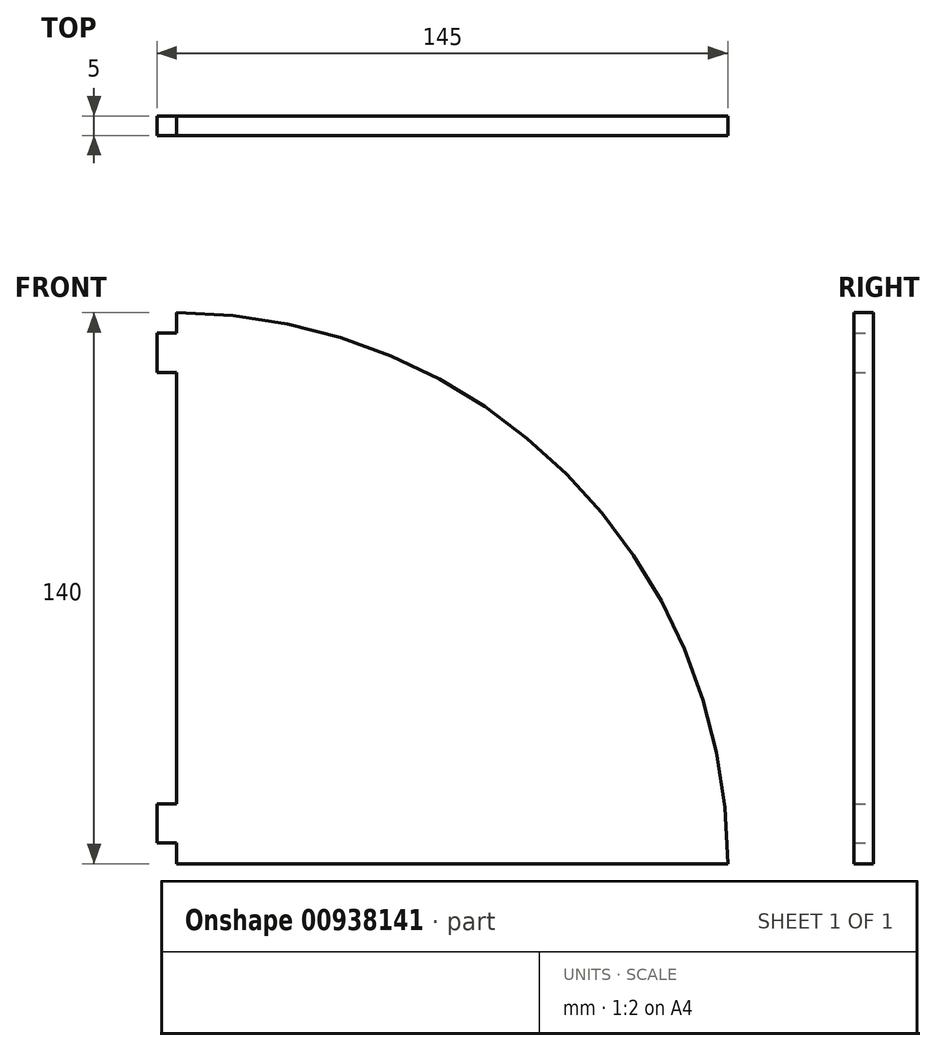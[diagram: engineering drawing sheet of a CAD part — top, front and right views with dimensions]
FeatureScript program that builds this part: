
annotation { "Feature Type Name" : "Feature", "Feature Type Description" : "" }
export const myFeature = defineFeature(function(context is Context, id is Id, definition is map)
    precondition{}
    {
        {
            var Q0;
            Q0=qCreatedBy(makeId("Front.planeOp"),FACE);
            var sketch = newSketch(context, id + "F0", { "sketchPlane" : qUnion([Q0])});
            skLineSegment(sketch, "E0.bottom", {"start": v(-70, 70) * mm, "end": v(-70, 70) * mm});
            skLineSegment(sketch, "E0.top", {"start": v(-70, -70) * mm, "end": v(70, -70) * mm});
            skLineSegment(sketch, "E0.left", {"start": v(-70, 70) * mm, "end": v(-70, -70) * mm});
            skLineSegment(sketch, "E0.right", {"start": v(70, -70) * mm, "end": v(70, -70) * mm});
            skPoint(sketch, "E0.middle", {"position": v(0, 0) * mm});
            skPoint(sketch, "E1.visualSharp", {"position": v(70, 70) * mm});
            skArc(sketch, "E1.filletArc", {"start": v(70, -70) * mm, "mid": v(29, 29) * mm, "end": v(-70, 70) * mm});
            skLineSegment(sketch, "E2.bottom", {"start": v(-70, 64.77) * mm, "end": v(-75, 64.77) * mm});
            skLineSegment(sketch, "E2.top", {"start": v(-70, 54.77) * mm, "end": v(-75, 54.77) * mm});
            skLineSegment(sketch, "E2.left", {"start": v(-70, 64.77) * mm, "end": v(-70, 54.77) * mm});
            skLineSegment(sketch, "E2.right", {"start": v(-75, 64.77) * mm, "end": v(-75, 54.77) * mm});
            skLineSegment(sketch, "E3.MirrorCS", {"start": v(-75, -64.77) * mm, "end": v(-75, -54.77) * mm});
            skLineSegment(sketch, "E4.MirrorCS", {"start": v(-70, -54.77) * mm, "end": v(-75, -54.77) * mm});
            skLineSegment(sketch, "E5.MirrorCS", {"start": v(-70, -64.77) * mm, "end": v(-75, -64.77) * mm});
            skSolve(sketch);
        }
        {
            var Q0;
            Q0 = qSketchRegion(id + "F0", true);
            extrude(context, id + "F1", {"entities" : qUnion([Q0]), "depth" : 5 * mm, "offsetDistance" : 25 * mm});
        }
    });
